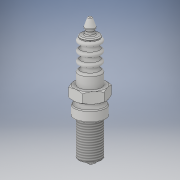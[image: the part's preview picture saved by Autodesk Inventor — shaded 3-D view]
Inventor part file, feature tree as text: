
AUTODESK INVENTOR PART (.ipt)
format: ipt  version: 2018 (Build 220112000, 112)  size: 445,440 bytes
history: native  units: mm
features: sketch x9, extrude x4, revolve x3, fillet x2, projected_geometry x2, plane x1, sweep x1, thread x1
ambient origin geometry x8: Origin, YZ Plane, XZ Plane, XY Plane, X Axis, Y Axis, Z Axis, Center Point
bodies: Solid1 (feature_tree), Solid2 (feature_tree), Solid3 (feature_tree)
feature tree (23):
  revolve  "Revolution1"  [1 undecoded]
  revolve  "Revolution2"  [1 undecoded]
  plane  "Work Plane1"
  extrude  "Extrusion1"  Depth=0.25mm
  revolve  "Revolution3"  [1 undecoded]
  extrude  "Extrusion2"  Depth=2.0mm
  extrude  "Extrusion3"  TaperAngle=90.0deg  [1 undecoded]
  extrude  "Extrusion4"  Depth=0.25mm
  sweep  "Sweep1"
  fillet  "Fillet1"  Radius=0.9mm
  fillet  "Fillet2"  Radius=11.419689mm
  thread  "Thread1"  [1 undecoded]
  sketch  "Sketch1"  dims[d0=17.5mm d1=2.0mm]
  sketch  "Sketch2"  dims[d2=1.0mm d3=60.0mm d5=1.0mm d6=10.0mm d8=10.0mm]
  sketch  "Sketch3"  dims[d10=20.0mm d12=1.0mm d13=10.0mm d15=10.0mm d17=0.25mm]
  sketch  "Sketch4"  dims[d18=0.25mm d19=1.75mm]
  sketch  "Sketch5"  dims[d20=0.04mm d21=2.0mm]
  sketch  "Sketch6"  dims[d22=7.0mm d23=90.0deg]
  sketch  "Sketch7"  dims[d24=0.083mm d25=0.25mm]
  sketch  "Sketch8"  dims[d26=2.125mm d27=3.42mm d28=0.9mm d29=11.419689mm d30=3.413864mm]
  projected_geometry  "Projected Loop1"
  sketch  "Sketch9"  dims[d31=2.01mm d32=0.25mm d33=0.620228mm d34=90.0deg d35=-14.0mm d36=3.9mm d37=2.4mm d38=0.0mm d39=11.0mm d40=1.2mm d41=3.35mm d43=0.25mm d44=90.0deg d45=4100.0mm d46=0.0mm d47=100.0mm d48=60.0deg d49=25.0mm d50=50.0mm d51=60.0deg d52=0.0mm d53=0.5mm d54=1.4mm d55=1.0mm d56=0.0mm d57=1.0mm d58=3.0mm d59=8.0mm d60=8.0mm d61=0.0mm d62=0.0mm d63=0.15mm d64=0.25mm d65=10.0mm d66=0.0mm]
  projected_geometry  "Project Cut Edges1"
note: 5 required parameter values undecoded (feature->parameter linkage not recoverable at this tier; creation-order binding heuristic only, values carry confidence <= 0.55)